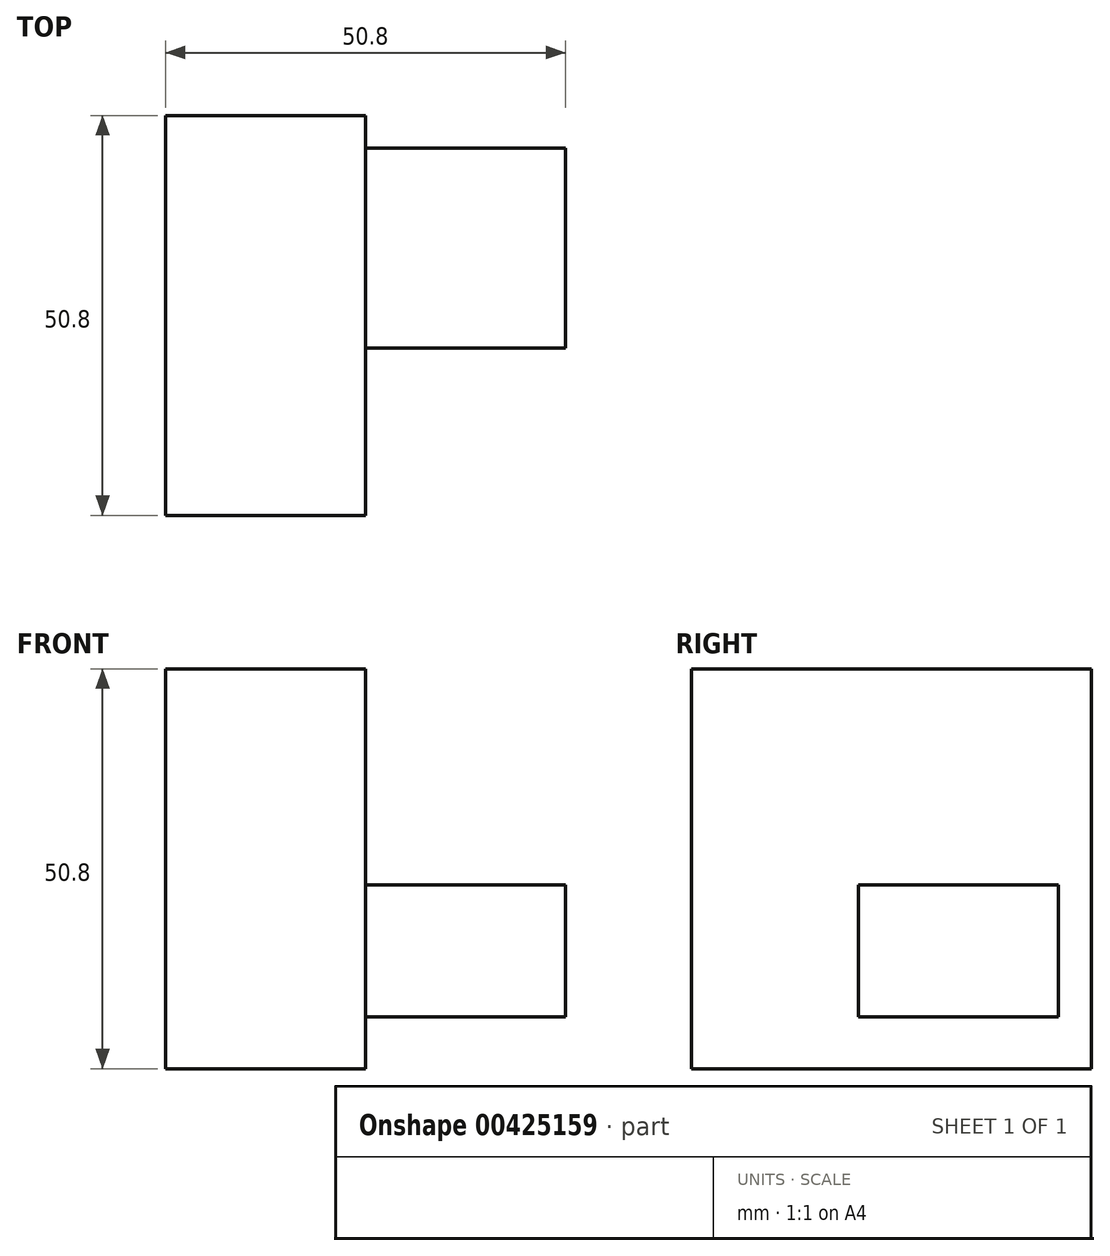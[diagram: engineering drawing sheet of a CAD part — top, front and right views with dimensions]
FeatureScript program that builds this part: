
annotation { "Feature Type Name" : "Feature", "Feature Type Description" : "" }
export const myFeature = defineFeature(function(context is Context, id is Id, definition is map)
    precondition{}
    {
        {
            var Q0;
            Q0=qCreatedBy(makeId("Front.planeOp"),FACE);
            var sketch = newSketch(context, id + "F0", { "sketchPlane" : qUnion([Q0])});
            skPoint(sketch, "E0.right.end.orphan", {"position": v(36.88, 0) * mm});
            skLineSegment(sketch, "E1.bottom", {"start": v(0, 0) * mm, "end": v(25.4, 0) * mm});
            skLineSegment(sketch, "E1.top", {"start": v(0, 50.8) * mm, "end": v(25.4, 50.8) * mm});
            skLineSegment(sketch, "E1.left", {"start": v(0, 0) * mm, "end": v(0, 50.8) * mm});
            skLineSegment(sketch, "E1.right", {"start": v(25.4, 0) * mm, "end": v(25.4, 50.8) * mm});
            skSolve(sketch);
        }
        {
            var Q0;
            Q0 = qSketchRegion(id + "F0", true);
            extrude(context, id + "F1", {"entities" : qUnion([Q0]), "depth" : 50.8 * mm});
        }
        {
            var Q0;
            Q0=qCreatedBy(makeId("Right.planeOp"),FACE);
            var sketch = newSketch(context, id + "F2", { "sketchPlane" : qUnion([Q0])});
            skLineSegment(sketch, "E2.bottom", {"start": v(-4.17, 23.32) * mm, "end": v(-29.57, 23.32) * mm});
            skLineSegment(sketch, "E2.top", {"start": v(-4.17, 6.55) * mm, "end": v(-29.57, 6.55) * mm});
            skLineSegment(sketch, "E2.left", {"start": v(-4.17, 23.32) * mm, "end": v(-4.17, 6.55) * mm});
            skLineSegment(sketch, "E2.right", {"start": v(-29.57, 23.32) * mm, "end": v(-29.57, 6.55) * mm});
            skSolve(sketch);
        }
        {
            var Q0;
            Q0 = qSketchRegion(id + "F2", true);
            extrude(context, id + "F3", {"entities" : qUnion([Q0]), "operationType" : NewBodyOperationType.ADD, "depth" : 50.8 * mm});
        }
    });
